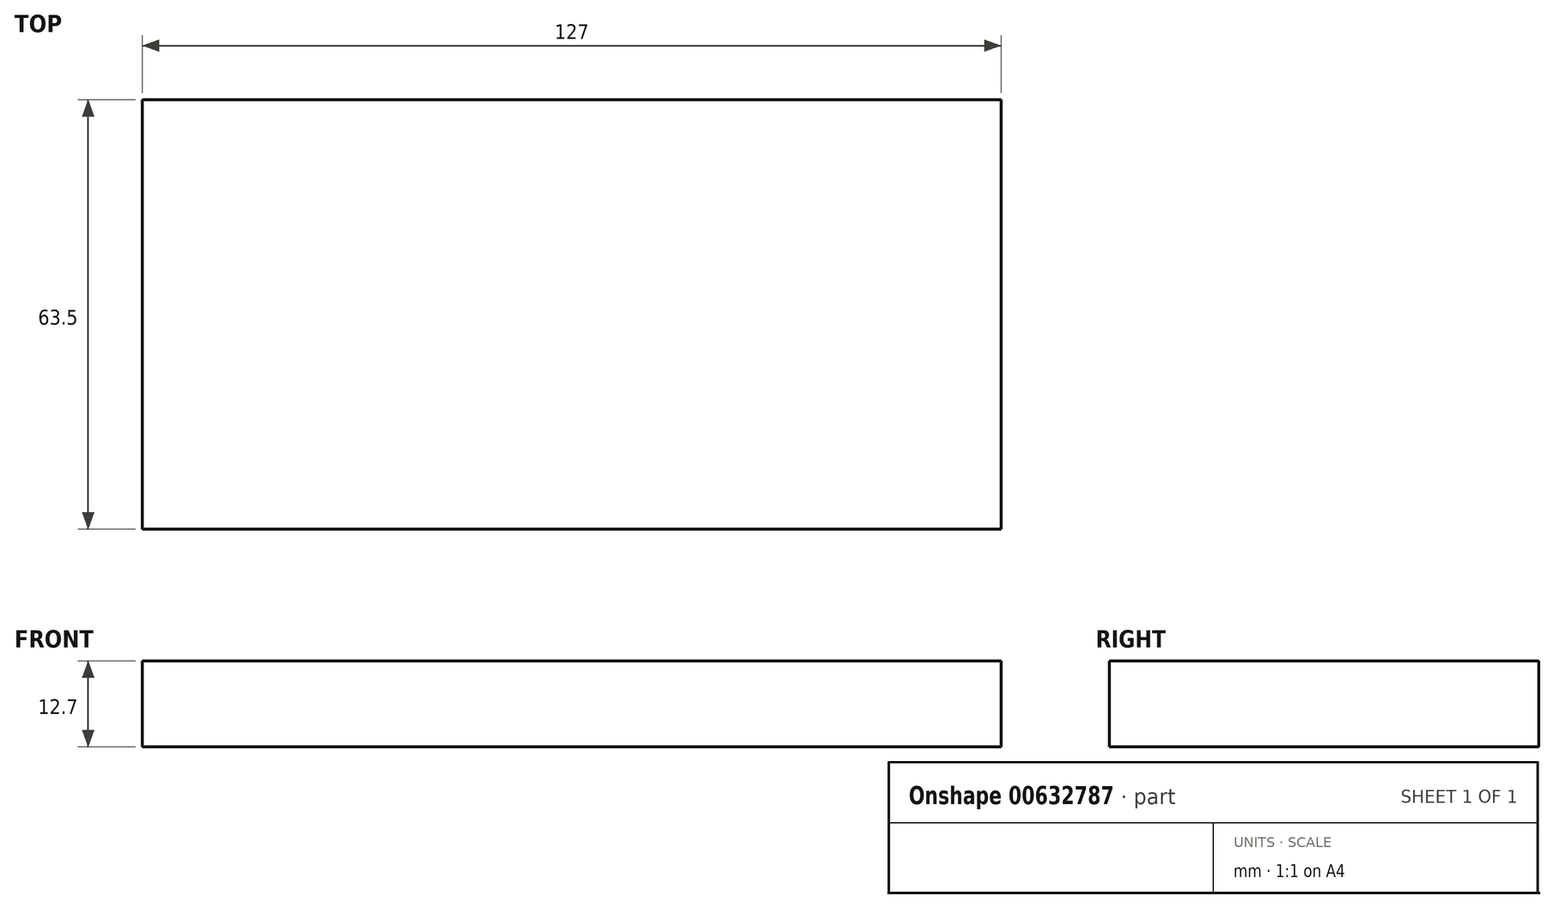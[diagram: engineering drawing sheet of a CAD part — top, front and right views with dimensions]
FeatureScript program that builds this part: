
annotation { "Feature Type Name" : "Feature", "Feature Type Description" : "" }
export const myFeature = defineFeature(function(context is Context, id is Id, definition is map)
    precondition{}
    {
        {
            var Q0;
            Q0=qCreatedBy(makeId("Top.planeOp"),FACE);
            var sketch = newSketch(context, id + "F0", { "sketchPlane" : qUnion([Q0])});
            skLineSegment(sketch, "E0.bottom", {"start": v(-56.92, 33.31) * mm, "end": v(70.08, 33.31) * mm});
            skLineSegment(sketch, "E0.top", {"start": v(-56.92, -30.19) * mm, "end": v(70.08, -30.19) * mm});
            skLineSegment(sketch, "E0.left", {"start": v(-56.92, 33.31) * mm, "end": v(-56.92, -30.19) * mm});
            skLineSegment(sketch, "E0.right", {"start": v(70.08, 33.31) * mm, "end": v(70.08, -30.19) * mm});
            skSolve(sketch);
        }
        {
            var Q0;
            Q0 = qSketchRegion(id + "F0", true);
            extrude(context, id + "F1", {"entities" : qUnion([Q0]), "depth" : 12.7 * mm, "offsetDistance" : 25.4 * mm});
        }
    });
